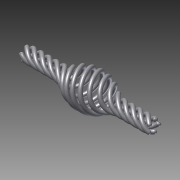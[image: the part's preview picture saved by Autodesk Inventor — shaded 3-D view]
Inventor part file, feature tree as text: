
AUTODESK INVENTOR PART (.ipt)
format: ipt  version: 2011 SP2 (Build 150309200, 309)  size: 953,344 bytes
history: native  units: mm
features: sketch x6, revolve x3, other x3, plane x2, sweep x1, pattern_circular x1, helix x1
ambient origin geometry x8: Origin, YZ Plane, XZ Plane, XY Plane, X Axis, Y Axis, Z Axis, Center Point
bodies: Solid1 (feature_tree)
feature tree (17):
  plane  "Work Plane1"
  sketch  "3D Sketch1"
  plane  "Work Plane2"
  sweep  "Sweep1"
  revolve  "Revolution1"  [1 undecoded]
  revolve  "Revolution2"  Angle=90.0deg
  pattern_circular  "Circular Pattern1"  Count=5  [1 undecoded]
  sketch  "Sketch1"  dims[d0=50.0mm d1=8.5mm]
  other  "Srf1"
  sketch  "Sketch2"  dims[d2=40.0mm d3=200.0mm]
  other  "Srf2"
  sketch  "Sketch3"  dims[d4=25.0mm d5=90.0deg]
  sketch  "Sketch4"  dims[d6=-100.0mm d7=50.0mm]
  sketch  "Sketch5"  dims[d8=60.0mm d9=200.0mm d10=10.0mm d11=0.0mm d12=90.0deg d13=90.0deg d14=0.0mm d15=0.0mm d16=3.0mm d17=0.0mm d18=90.0deg d19=90.0deg d20=50.0mm d21=360.0deg]
  revolve  "RevolutionSrf1"  [1 undecoded]
  helix  "Coil1"  [1 undecoded]
  other  "3D Intersection1"
note: 4 required parameter values undecoded (feature->parameter linkage not recoverable at this tier; creation-order binding heuristic only, values carry confidence <= 0.55)